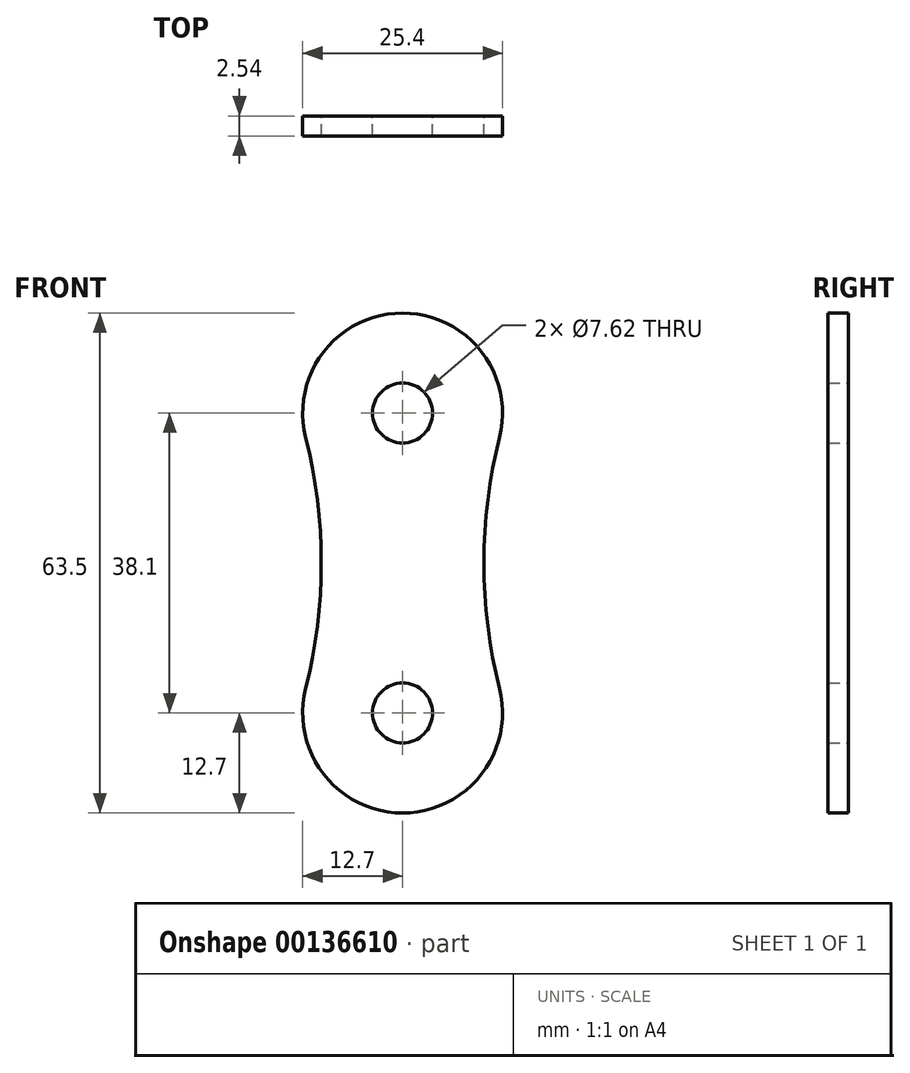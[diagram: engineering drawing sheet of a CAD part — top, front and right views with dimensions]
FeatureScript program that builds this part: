
annotation { "Feature Type Name" : "Feature", "Feature Type Description" : "" }
export const myFeature = defineFeature(function(context is Context, id is Id, definition is map)
    precondition{}
    {
        {
            var Q0;
            Q0=qCreatedBy(makeId("Front.planeOp"),FACE);
            var sketch = newSketch(context, id + "F0", { "sketchPlane" : qUnion([Q0])});
            skArc(sketch, "E0", {"start": v(12.31, 15.94) * mm, "mid": v(0, 31.75) * mm, "end": v(-12.31, 15.94) * mm});
            skArc(sketch, "E1", {"start": v(-12.31, -15.94) * mm, "mid": v(0, -31.75) * mm, "end": v(12.31, -15.94) * mm});
            skCircle(sketch, "E2", {"center": v(0, 19.05) * mm, "radius": 3.81 * mm});
            skCircle(sketch, "E3", {"center": v(0, -19.05) * mm, "radius": 3.81 * mm});
            skArc(sketch, "E4", {"start": v(-12.31, -15.94) * mm, "mid": v(-10.33, 0) * mm, "end": v(-12.31, 15.94) * mm});
            skArc(sketch, "E5.MirrorCS", {"start": v(12.31, -15.94) * mm, "mid": v(10.33, 0) * mm, "end": v(12.31, 15.94) * mm});
            skSolve(sketch);
        }
        {
            var Q0;
            Q0 = qSketchRegion(id + "F0", true);
            var Q1;
            Q1=makeQuery(id+"F0.imprint","IMPRINT",FACE,{"disambiguationData":[TD([[makeQuery(id+"F0.imprint","IMPRINT",EDGE,{"derivedFrom":sQuery(id+"F0.wireOp",EDGE,"E0")}),1.0]])]});
            extrude(context, id + "F1", {"entities" : qUnion([Q0, Q1]), "depth" : 2.54 * mm});
        }
    });
